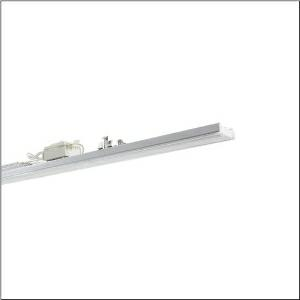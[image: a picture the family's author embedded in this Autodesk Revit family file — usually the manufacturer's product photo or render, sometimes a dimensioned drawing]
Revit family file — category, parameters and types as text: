
# Revit family: licross_21_recessed_mo_52tl10dn4axg
name_source: partatom
category: Lighting Fixtures
units: mm (PartAtom-declared; Revit-internal decimal feet)

## family parameters
Cut with Voids When Loaded = No
Host = Face
Light Source = No
Part Type = Normal
Room Calculation Point = No
Round Connector Dimension = Use Diameter
Shared = No

## types (1)
- --- (1 x LED, 10000 lm, 58 W, 4000K)
    Apparent Load = 58 VA
    CIE Flux Codes = 50 81 96 100 100
    Color Rendering = 80
    Color Temperature = 4000K
    Default Elevation = 1800 mm
    Description = Licross 21 Recessed MO, luminaire insert, of sheet steel, galvanised, coil coated, white, length: 1.500mm, width: 66mm, height: 67mm, LED rated luminous flux: 10.000lm, light colour: 840, SDCM (Standard Deviation of Colour Matching)MacAdam ≤ 3 SDCM (initial), control gear: DALI 2, with plug, 5-pole, with phase selection, mains connection: 220..240V, AC, 50/60Hz, rated input power: 58W, internal wiring halogen-free, primary optical cover: cover, of PMMA, light emission: direct distribution, primary light characteristic: symmetric, protection rating (complete): IP40, insulation class (complete): insulation class I (protective earthing), certification: CE, ENEC, VDE, UKCA, protection symbol: D if used in an environment without relevant dust loads with corresponding accessories, impact resistance: IK06, permissible ambient temperature for indoor applications: -25..+35°C, corresponds to IFS (International Featured Standards) requirements for safety and quality in the food industry, reducing of maximum allowable ambient temperature of 5°C with ceiling mounting, LABS conformity tested according to VDMA 24364:2018-05, The light source and the operating device comply with the requirements of the Ecodesign Regulation (EU) 2019/2020 and are replaceable in accordance with this regulation, packaging unit: 1 piece
    Height = 58 mm
    Lamp = 1 x LED
    Lamp Light Flux = 10000 lm
    Lamp Power = 58 W
    Lamp count = 1
    Length = 1500 mm
    Luminous efficacy = 172 lm/W
    Manufacturer = Siteco
    ModVariant = No
    Model = 52TL10DN4AXG
    Mounting Place = Ceiling
    Mounting Type = Pendant
    Number of Poles = 1
    OnlyDefault = Yes
    Power Factor = 1
    Product Name = Licross 21 Recessed MO
    Product group = luminaire insert | ceiling pendant
    ProductGroupID = 901
    Protection Class = Protection class I
    Protection Degree = IP 40
    RLX_Detail_Level = 1
    RLX_Emergency_Light_Flux = 0 lm
    RLX_Emergency_Type = 0
    RLX_Emergency_Type_DB = No
    RlxData = <blob elided: 24693 chars, md5=4dc61e90>
    Socket = socket
    Standby Power = 0 W
    System Light Flux = 10000 lm
    System Power = 58 W
    Type Comments = factory setting: luminous flux: 100 % | dim-lin: 254 | 390 mA
    Type Image = l_1296930.jpg
    URL = http://relux.com
    VarID = @adj_127717
    Voltage = 0 V
    Weight = 0.00 kg
    Width = 66 mm

## geometry (parser evidence)
native form markers: Blend x4, Sweep x10
no freeform markers — native parametric forms only
